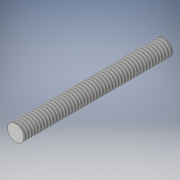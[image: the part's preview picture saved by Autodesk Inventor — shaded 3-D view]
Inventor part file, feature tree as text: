
AUTODESK INVENTOR PART (.ipt)
format: ipt  version: 2017 (Build 210142000, 142)  size: 100,352 bytes
history: native  units: in
note: dims shown in document units (in); Inventor stores cm internally (conversion verified against a paired STEP export)
features: extrude x2, sketch x2, thread x1
ambient origin geometry x8: Origin, YZ Plane, XZ Plane, XY Plane, X Axis, Y Axis, Z Axis, Center Point
bodies: Solid1 (feature_tree)
feature tree (5):
  extrude  "Extrusion1"  Depth=3.0in TaperAngle=0.0deg
  thread  "Thread1"  [1 undecoded]
  extrude  "Extrusion2"  [1 undecoded]
  sketch  "Sketch1"  dims[d0=0.164in d1=3.0in d2=0.0in d3=1.0in d4=0.0in]
  sketch  "Sketch2"  dims[d5=1.4961in d6=0.0in]
note: 2 required parameter values undecoded (feature->parameter linkage not recoverable at this tier; creation-order binding heuristic only, values carry confidence <= 0.55)
